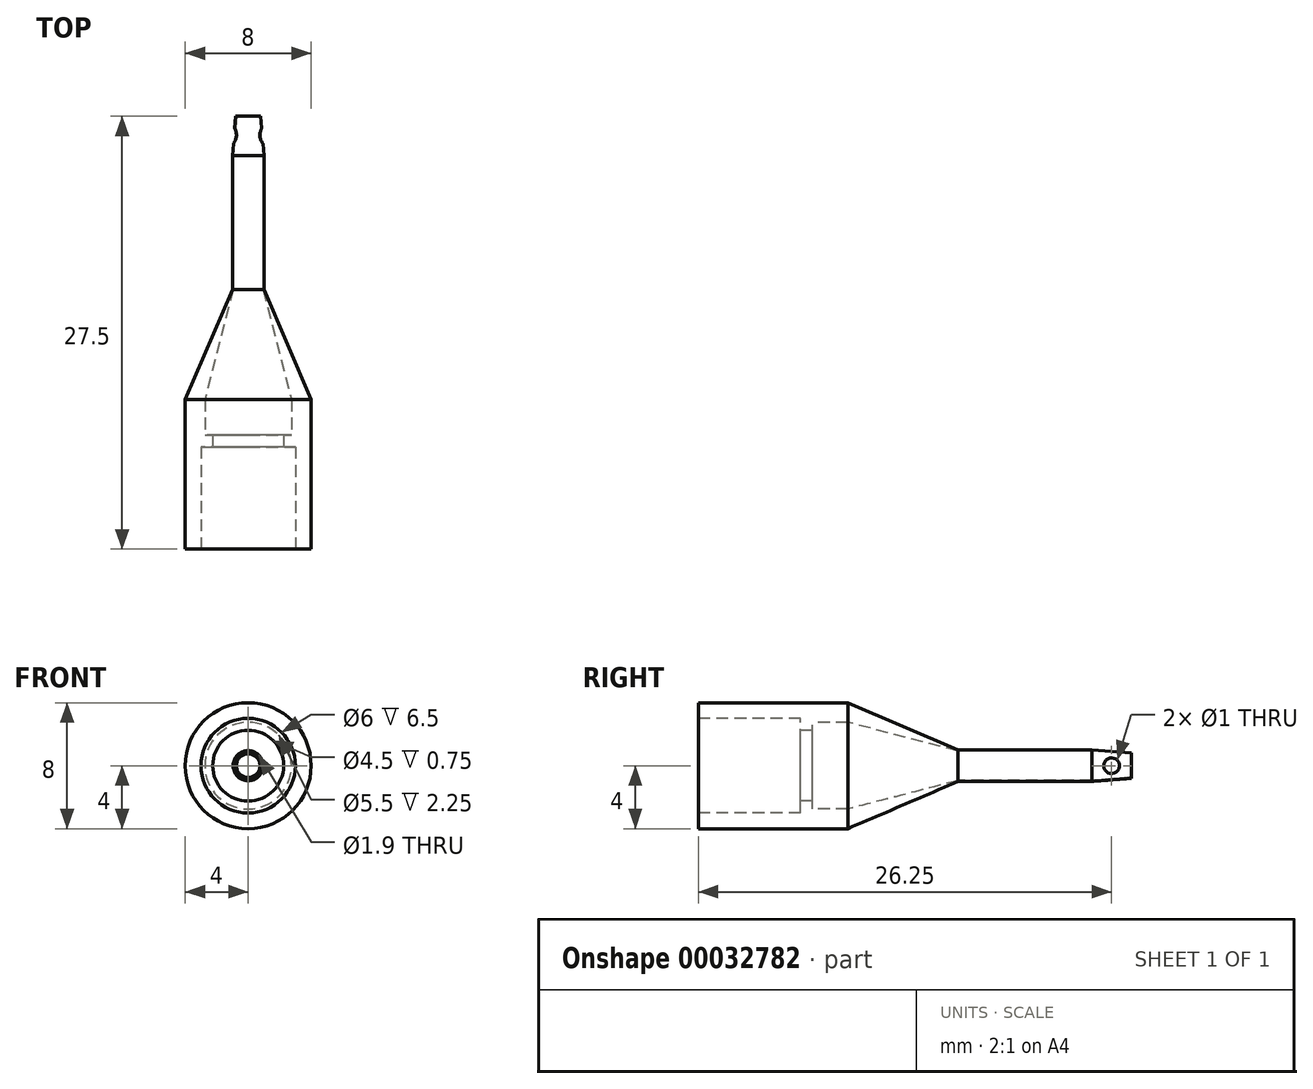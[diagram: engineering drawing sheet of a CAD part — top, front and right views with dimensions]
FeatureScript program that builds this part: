
annotation { "Feature Type Name" : "Feature", "Feature Type Description" : "" }
export const myFeature = defineFeature(function(context is Context, id is Id, definition is map)
    precondition{}
    {
        {
            var Q0;
            Q0=qCreatedBy(makeId("Right.planeOp"),FACE);
            var sketch = newSketch(context, id + "F0", { "sketchPlane" : qUnion([Q0])});
            skLineSegment(sketch, "E0", {"start": v(0, 3) * mm, "end": v(0, 4) * mm});
            skLineSegment(sketch, "E1", {"start": v(0, 4) * mm, "end": v(9.5, 4) * mm});
            skLineSegment(sketch, "E2", {"start": v(9.5, 4) * mm, "end": v(16.5, 1) * mm});
            skLineSegment(sketch, "E3", {"start": v(16.5, 1) * mm, "end": v(25, 1) * mm});
            skLineSegment(sketch, "E4", {"start": v(25, 1) * mm, "end": v(27.5, 0.8) * mm});
            skLineSegment(sketch, "E5", {"start": v(27.5, 0.8) * mm, "end": v(27.5, 0.75) * mm});
            skLineSegment(sketch, "E6", {"start": v(27.5, 0.75) * mm, "end": v(25, 0.95) * mm});
            skLineSegment(sketch, "E7", {"start": v(25, 0.95) * mm, "end": v(16.5, 0.95) * mm});
            skLineSegment(sketch, "E8", {"start": v(0, 3) * mm, "end": v(6.5, 3) * mm});
            skLineSegment(sketch, "E9", {"start": v(6.5, 3) * mm, "end": v(6.5, 2.25) * mm});
            skLineSegment(sketch, "E10", {"start": v(6.5, 2.25) * mm, "end": v(7.25, 2.25) * mm});
            skLineSegment(sketch, "E11", {"start": v(7.25, 2.25) * mm, "end": v(7.25, 2.75) * mm});
            skLineSegment(sketch, "E12", {"start": v(7.25, 2.75) * mm, "end": v(9.5, 2.75) * mm});
            skLineSegment(sketch, "E13", {"start": v(9.5, 2.75) * mm, "end": v(16.5, 0.95) * mm});
            skLineSegment(sketch, "E14", {"start": v(-9.43, 0) * mm, "end": v(41.47, 0) * mm});
            skSolve(sketch);
        }
        {
            var Q0;
            Q0=makeQuery(id+"F0.imprint","IMPRINT",FACE,{"disambiguationData":[TD([[makeQuery(id+"F0.imprint","IMPRINT",EDGE,{"derivedFrom":sQuery(id+"F0.wireOp",EDGE,"E0")}),-1.0]])]});
            var Q1;
            Q1=sQuery(id+"F0.wireOp",EDGE,"E14");
            revolve(context, id + "F1", {"entities" : qUnion([Q0]), "axis" : qUnion([Q1]), "revolveType" : RevolveType.FULL});
        }
        {
            var Q0;
            Q0=qCreatedBy(makeId("Right.planeOp"),FACE);
            var sketch = newSketch(context, id + "F2", { "sketchPlane" : qUnion([Q0])});
            skCircle(sketch, "E15", {"center": v(26.25, 0) * mm, "radius": 0.5 * mm});
            skSolve(sketch);
        }
        {
            var Q0;
            Q0 = qSketchRegion(id + "F2", true);
            extrude(context, id + "F3", {"entities" : qUnion([Q0]), "operationType" : NewBodyOperationType.REMOVE, "endBound" : BoundingType.SYMMETRIC, "oppositeDirection" : true, "depth" : 2 * mm});
        }
    });
